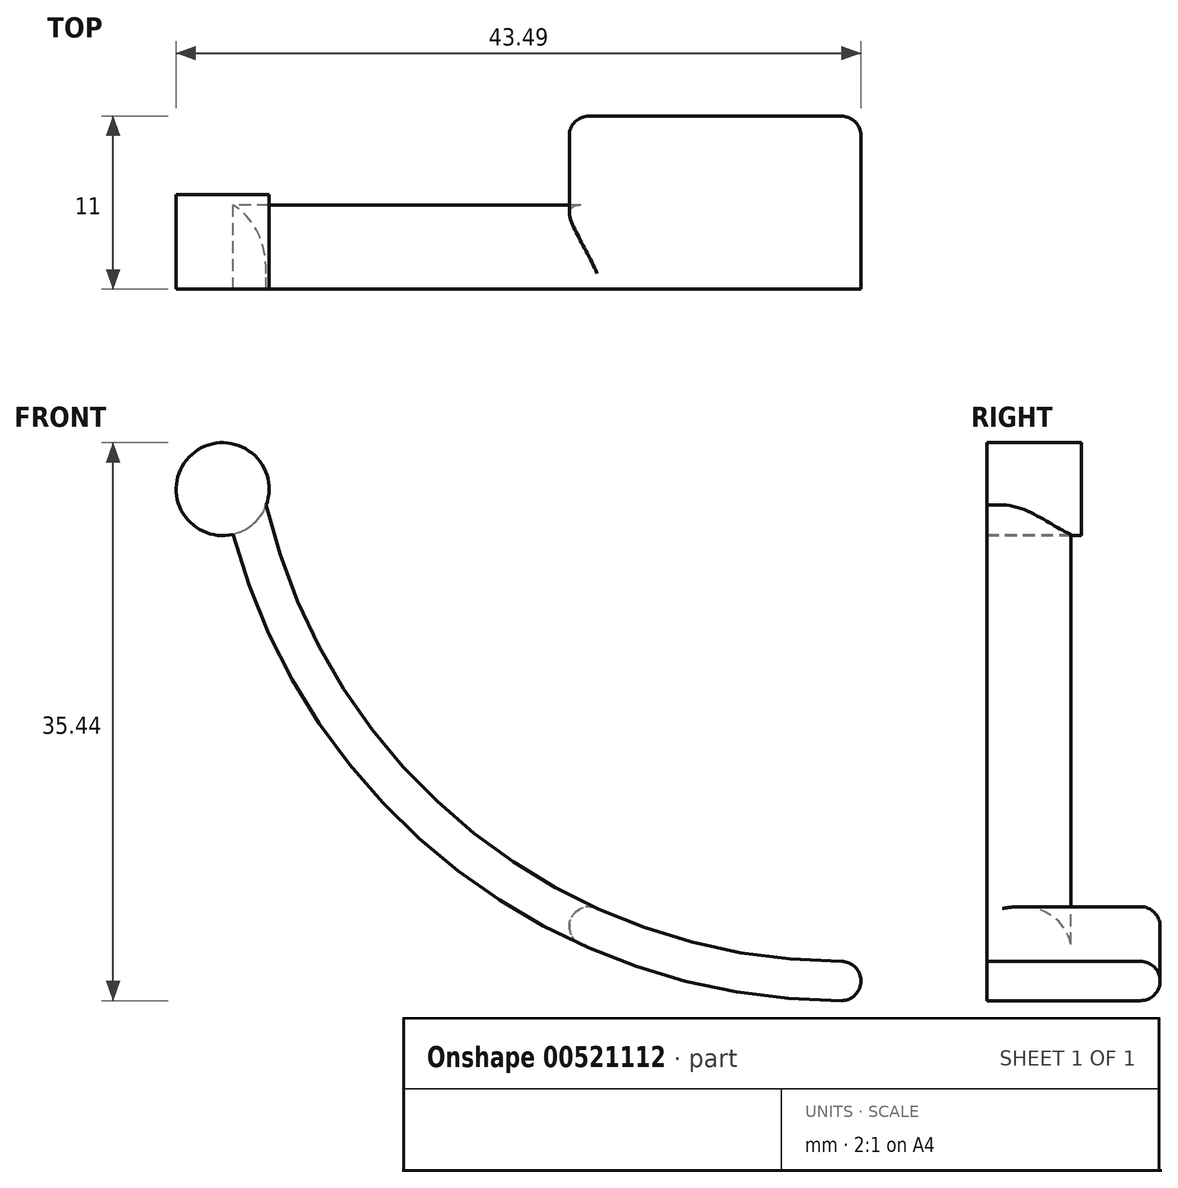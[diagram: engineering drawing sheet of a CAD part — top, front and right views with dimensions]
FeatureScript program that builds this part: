
annotation { "Feature Type Name" : "Feature", "Feature Type Description" : "" }
export const myFeature = defineFeature(function(context is Context, id is Id, definition is map)
    precondition{}
    {
        {
            var Q0;
            Q0=qCreatedBy(makeId("Front.planeOp"),FACE);
            var sketch = newSketch(context, id + "F0", { "sketchPlane" : qUnion([Q0])});
            skArc(sketch, "E0", {"start": v(-38.63, 29.62) * mm, "mid": v(-24.34, 8.26) * mm, "end": v(0, 0) * mm});
            skArc(sketch, "E1", {"start": v(-36.52, 31.48) * mm, "mid": v(-23.3, 10.62) * mm, "end": v(0, 2.5) * mm});
            skArc(sketch, "E2", {"start": v(-36.52, 31.48) * mm, "mid": v(-41.24, 34.7) * mm, "end": v(-38.63, 29.62) * mm});
            skArc(sketch, "E3", {"start": v(0, 0) * mm, "mid": v(1.25, 1.25) * mm, "end": v(0, 2.5) * mm});
            skSolve(sketch);
        }
        {
            var Q0;
            Q0 = qSketchRegion(id + "F0", true);
            extrude(context, id + "F1", {"entities" : qUnion([Q0]), "depth" : 6 * mm, "offsetDistance" : 25 * mm});
        }
        {
            var Q0;
            Q0=qCreatedBy(makeId("Front.planeOp"),FACE);
            var sketch = newSketch(context, id + "F2", { "sketchPlane" : qUnion([Q0])});
            skArc(sketch, "E4", {"start": v(-15.5, 5.85) * mm, "mid": v(-7.93, 3.35) * mm, "end": v(0, 2.5) * mm});
            skArc(sketch, "E5", {"start": v(-16.54, 3.58) * mm, "mid": v(-8.46, 0.9) * mm, "end": v(0, 0) * mm});
            skArc(sketch, "E6", {"start": v(0, 0) * mm, "mid": v(1.25, 1.25) * mm, "end": v(0, 2.5) * mm});
            skArc(sketch, "E7", {"start": v(-15.5, 5.85) * mm, "mid": v(-17.16, 5.23) * mm, "end": v(-16.54, 3.58) * mm});
            skSolve(sketch);
        }
        {
            var Q0;
            Q0 = qSketchRegion(id + "F2", true);
            extrude(context, id + "F3", {"entities" : qUnion([Q0]), "operationType" : NewBodyOperationType.ADD, "oppositeDirection" : true, "depth" : 5 * mm, "offsetDistance" : 25 * mm});
        }
        {
            var Q0;
            Q0=makeQuery(id+"F3.opExtrude","CAP_EDGE",EDGE,{"disambiguationData":[OSD([sQuery(id+"F2.wireOp",EDGE,"E6")])],"isStart":false});
            fillet(context, id + "F4", {"entities" : qUnion([Q0]), "radius" : 1.25 * mm, "tangentPropagation" : true, "allowEdgeOverflow" : false});
        }
        {
            var Q0;
            Q0=makeQuery(id+"F3.boolean.opBoolean","SPLIT",EDGE,{"derivedFrom":makeQuery(id+"F1.opExtrude","CAP_EDGE",EDGE,{"disambiguationData":[OSD([sQuery(id+"F0.wireOp",EDGE,"E1")])],"isStart":true})});
            fillet(context, id + "F5", {"entities" : qUnion([Q0]), "radius" : 5 * mm, "tangentPropagation" : true, "allowEdgeOverflow" : false});
        }
    });
